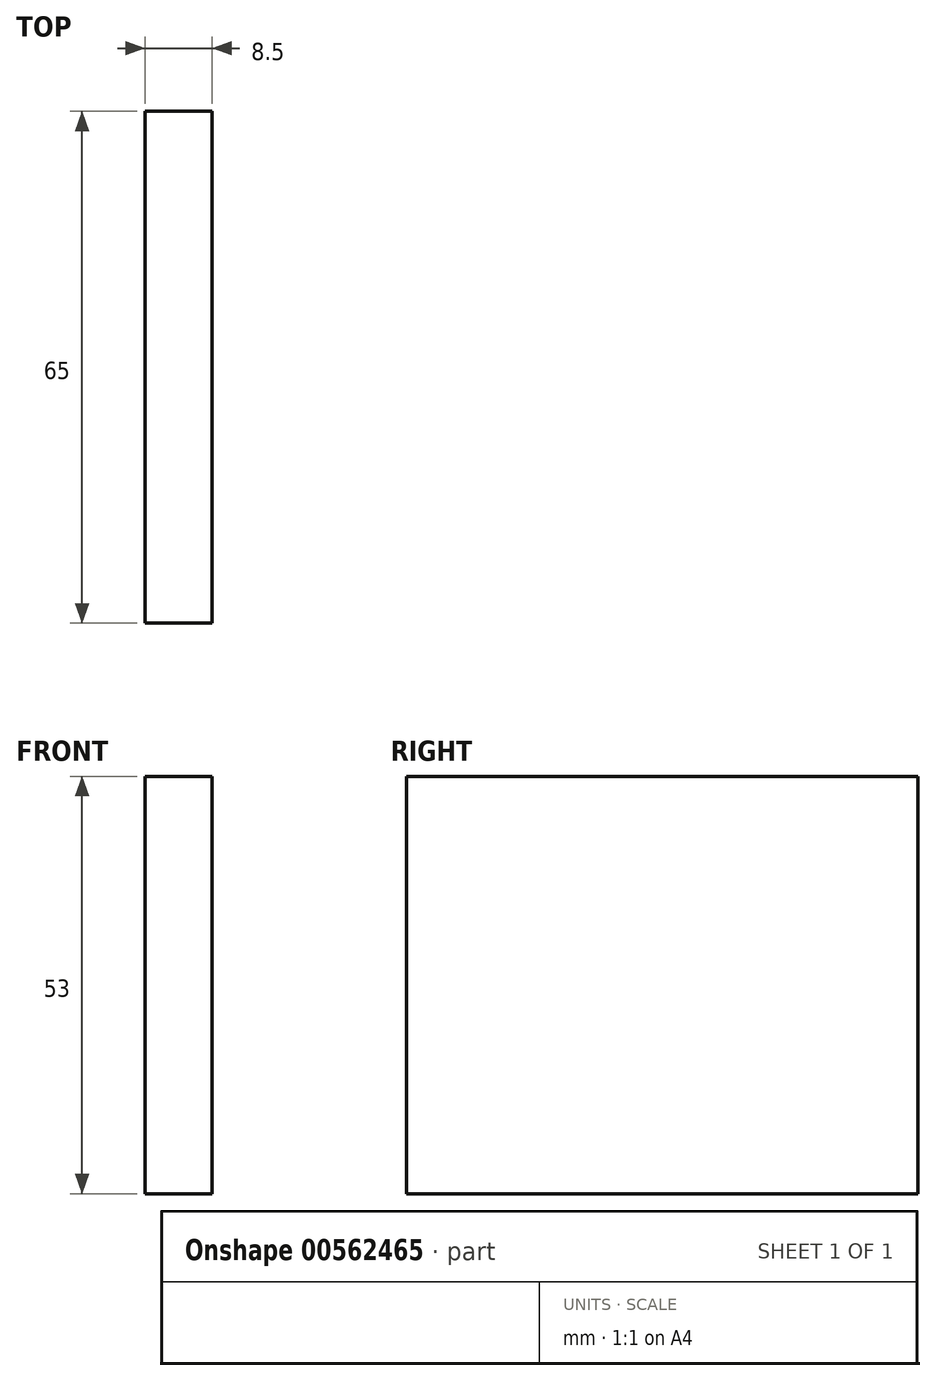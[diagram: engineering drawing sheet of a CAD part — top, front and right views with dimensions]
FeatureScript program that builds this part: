
annotation { "Feature Type Name" : "Feature", "Feature Type Description" : "" }
export const myFeature = defineFeature(function(context is Context, id is Id, definition is map)
    precondition{}
    {
        {
            var Q0;
            Q0=qCreatedBy(makeId("Right.planeOp"),FACE);
            var sketch = newSketch(context, id + "F0", { "sketchPlane" : qUnion([Q0])});
            skLineSegment(sketch, "E0.bottom", {"start": v(-32.5, 26.5) * mm, "end": v(32.5, 26.5) * mm});
            skLineSegment(sketch, "E0.top", {"start": v(-32.5, -26.5) * mm, "end": v(32.5, -26.5) * mm});
            skLineSegment(sketch, "E0.left", {"start": v(-32.5, 26.5) * mm, "end": v(-32.5, -26.5) * mm});
            skLineSegment(sketch, "E0.right", {"start": v(32.5, 26.5) * mm, "end": v(32.5, -26.5) * mm});
            skPoint(sketch, "E0.middle", {"position": v(0, 0) * mm});
            skSolve(sketch);
        }
        {
            var Q0;
            Q0=makeQuery(id+"F0.imprint","IMPRINT",FACE,{"disambiguationData":[TD([[makeQuery(id+"F0.imprint","IMPRINT",EDGE,{"derivedFrom":sQuery(id+"F0.wireOp",EDGE,"E0.bottom")}),-1.0]])]});
            extrude(context, id + "F1", {"entities" : qUnion([Q0]), "depth" : 8.5 * mm, "offsetDistance" : 25 * mm, "symmetric" : true});
        }
    });
